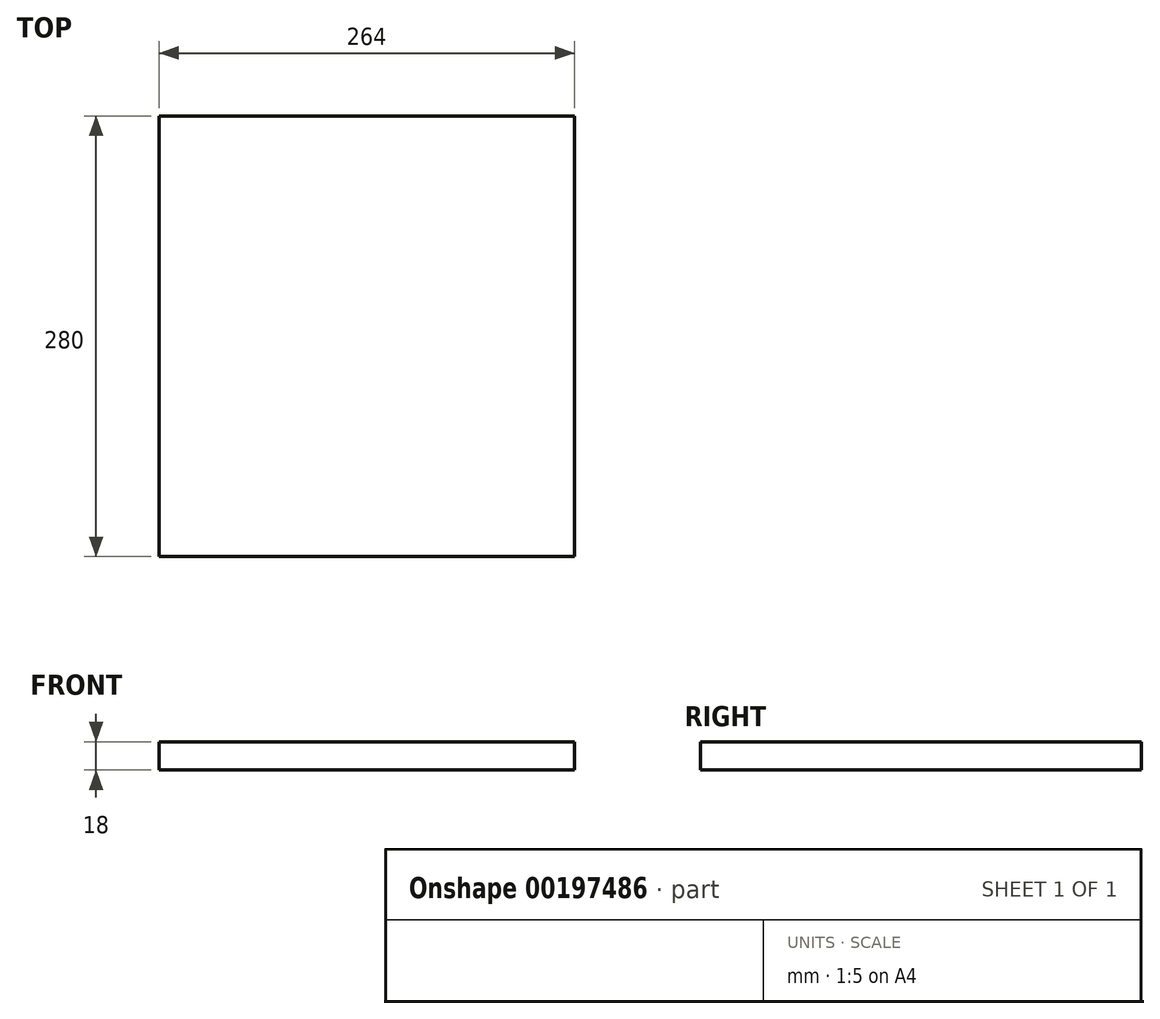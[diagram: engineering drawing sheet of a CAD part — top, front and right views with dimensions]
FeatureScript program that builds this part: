
annotation { "Feature Type Name" : "Feature", "Feature Type Description" : "" }
export const myFeature = defineFeature(function(context is Context, id is Id, definition is map)
    precondition{}
    {
        {
            var Q0;
            Q0=qCreatedBy(makeId("Top.planeOp"),FACE);
            var sketch = newSketch(context, id + "F0", { "sketchPlane" : qUnion([Q0])});
            skLineSegment(sketch, "E0.bottom", {"start": v(132, -140) * mm, "end": v(-132, -140) * mm});
            skLineSegment(sketch, "E0.top", {"start": v(132, 140) * mm, "end": v(-132, 140) * mm});
            skLineSegment(sketch, "E0.left", {"start": v(132, -140) * mm, "end": v(132, 140) * mm});
            skLineSegment(sketch, "E0.right", {"start": v(-132, -140) * mm, "end": v(-132, 140) * mm});
            skPoint(sketch, "E0.middle", {"position": v(0, 0) * mm});
            skSolve(sketch);
        }
        {
            var Q0;
            Q0 = qSketchRegion(id + "F0", true);
            extrude(context, id + "F1", {"entities" : qUnion([Q0]), "depth" : 18 * mm});
        }
    });
